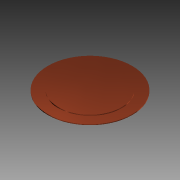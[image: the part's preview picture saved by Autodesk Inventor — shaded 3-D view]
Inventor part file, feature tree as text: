
AUTODESK INVENTOR PART (.ipt)
format: ipt  version: 2014 (Build 180170000, 170)  size: 80,896 bytes
history: native  units: in
note: dims shown in document units (in); Inventor stores cm internally (conversion verified against a paired STEP export)
features: revolve x1, sketch x1
ambient origin geometry x8: Origin, YZ Plane, XZ Plane, XY Plane, X Axis, Y Axis, Z Axis, Center Point
bodies: Solid1 (feature_tree)
feature tree (2):
  revolve  "Revolution1"  [1 undecoded]
  sketch  "Sketch1"  dims[d0=0.2362in d1=0.0039in d2=0.1772in d3=0.0047in d4=90.0deg]
note: 1 required parameter value undecoded (feature->parameter linkage not recoverable at this tier; creation-order binding heuristic only, values carry confidence <= 0.55)
